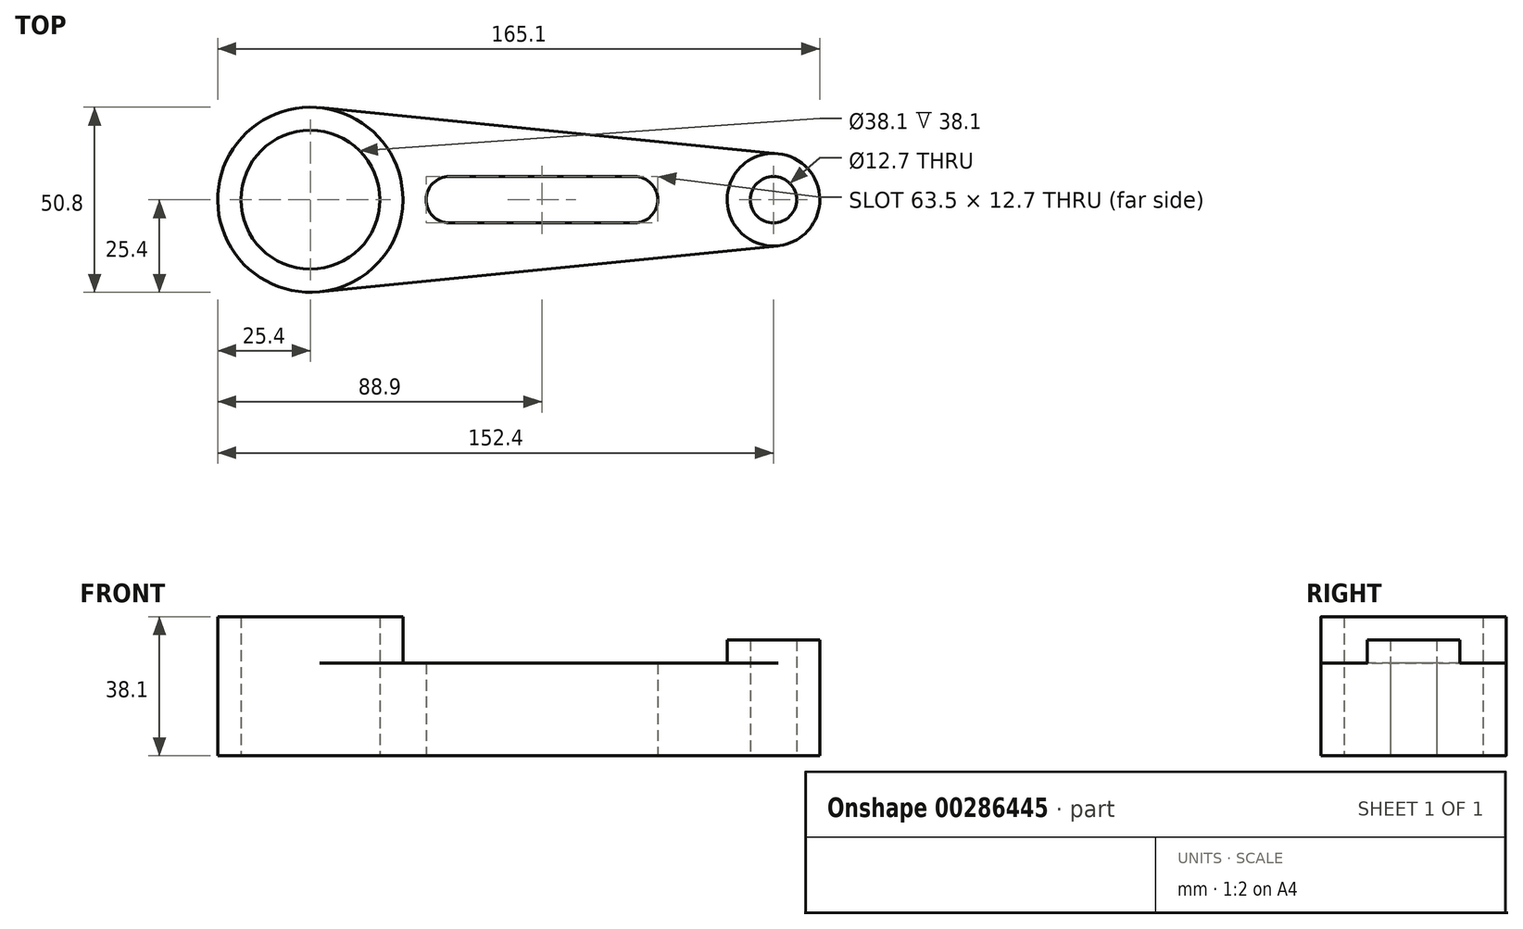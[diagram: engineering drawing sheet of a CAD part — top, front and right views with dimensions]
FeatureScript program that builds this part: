
annotation { "Feature Type Name" : "Feature", "Feature Type Description" : "" }
export const myFeature = defineFeature(function(context is Context, id is Id, definition is map)
    precondition{}
    {
        {
            var Q0;
            Q0=qCreatedBy(makeId("Top.planeOp"),FACE);
            var sketch = newSketch(context, id + "F0", { "sketchPlane" : qUnion([Q0])});
            skCircle(sketch, "E0", {"center": v(-38.1, 0) * mm, "radius": 25.4 * mm});
            skCircle(sketch, "E1", {"center": v(-38.1, 0) * mm, "radius": 19.05 * mm});
            skCircle(sketch, "E2", {"center": v(88.9, 0) * mm, "radius": 12.7 * mm});
            skCircle(sketch, "E3", {"center": v(88.9, 0) * mm, "radius": 6.35 * mm});
            skArc(sketch, "E4", {"start": v(0, 6.35) * mm, "mid": v(-6.35, 0) * mm, "end": v(0, -6.35) * mm});
            skLineSegment(sketch, "E5", {"start": v(0, 6.35) * mm, "end": v(50.8, 6.35) * mm});
            skArc(sketch, "E6", {"start": v(50.8, 6.35) * mm, "mid": v(57.15, 0) * mm, "end": v(50.8, -6.35) * mm});
            skLineSegment(sketch, "E7", {"start": v(0, -6.35) * mm, "end": v(50.8, -6.35) * mm});
            skLineSegment(sketch, "E8", {"start": v(-35.56, 25.27) * mm, "end": v(90.17, 12.64) * mm});
            skLineSegment(sketch, "E9", {"start": v(-35.56, -25.27) * mm, "end": v(90.17, -12.64) * mm});
            skSolve(sketch);
        }
        {
            var Q0;
            Q0=makeQuery(id+"F0.imprint","IMPRINT",FACE,{"disambiguationData":[TD([[makeQuery(id+"F0.imprint","IMPRINT",EDGE,{"derivedFrom":sQuery(id+"F0.wireOp",EDGE,"E1")}),-1.0]])]});
            extrude(context, id + "F1", {"entities" : qUnion([Q0]), "depth" : 38.1 * mm});
        }
        {
            var Q0;
            Q0=makeQuery(id+"F0.imprint","IMPRINT",FACE,{"disambiguationData":[TD([[makeQuery(id+"F0.imprint","IMPRINT",EDGE,{"derivedFrom":sQuery(id+"F0.wireOp",EDGE,"E4")}),-1.0]])]});
            extrude(context, id + "F2", {"entities" : qUnion([Q0]), "operationType" : NewBodyOperationType.ADD, "depth" : 25.4 * mm});
        }
        {
            var Q0;
            Q0=makeQuery(id+"F0.imprint","IMPRINT",FACE,{"disambiguationData":[TD([[makeQuery(id+"F0.imprint","IMPRINT",EDGE,{"derivedFrom":sQuery(id+"F0.wireOp",EDGE,"E3")}),-1.0]])]});
            extrude(context, id + "F3", {"entities" : qUnion([Q0]), "operationType" : NewBodyOperationType.ADD, "depth" : 31.75 * mm});
        }
    });
